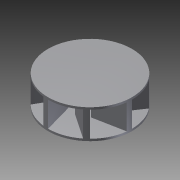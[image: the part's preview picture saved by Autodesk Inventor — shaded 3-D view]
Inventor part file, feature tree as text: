
AUTODESK INVENTOR PART (.ipt)
format: ipt  version: 2012 (Build 160160000, 160)  size: 138,752 bytes
history: native  units: in
note: dims shown in document units (in); Inventor stores cm internally (conversion verified against a paired STEP export)
features: extrude x3, sketch x3, plane x1
ambient origin geometry x8: Origin, YZ Plane, XZ Plane, XY Plane, X Axis, Y Axis, Z Axis, Center Point
bodies: Solid1 (feature_tree)
feature tree (7):
  extrude  "Extrusion1"  Depth=0.1in TaperAngle=0.0deg
  extrude  "Extrusion2"  Depth=1.2in TaperAngle=0.0deg
  plane  "Work Plane1"
  extrude  "Extrusion3"  Depth=4.0in
  sketch  "Sketch1"  dims[d0=4.0in d1=0.1in d2=0.0in]
  sketch  "Sketch2"  dims[d5=3.1496in d7=360.0deg d9=1.2in d10=0.0in]
  sketch  "Sketch3"  dims[d11=1.4in d12=4.0in d13=0.1in d14=0.0in]
